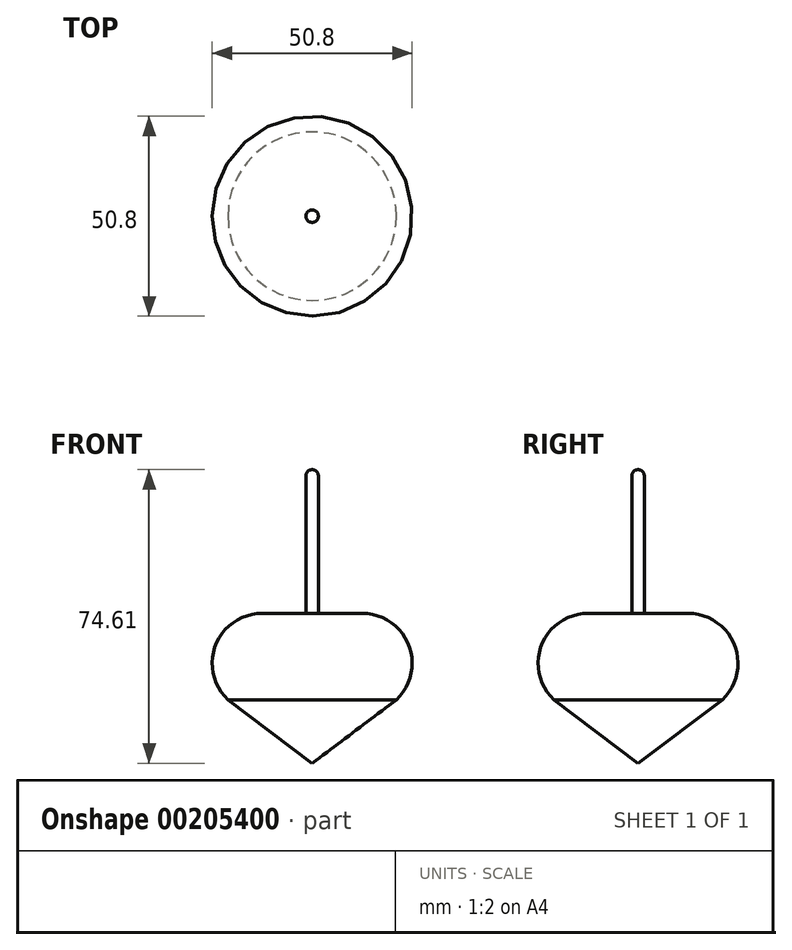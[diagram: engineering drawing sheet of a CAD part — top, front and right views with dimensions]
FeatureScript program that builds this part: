
annotation { "Feature Type Name" : "Feature", "Feature Type Description" : "" }
export const myFeature = defineFeature(function(context is Context, id is Id, definition is map)
    precondition{}
    {
        {
            var Q0;
            Q0=qCreatedBy(makeId("Front.planeOp"),FACE);
            var sketch = newSketch(context, id + "F0", { "sketchPlane" : qUnion([Q0])});
            skLineSegment(sketch, "E0", {"start": v(0, 0) * mm, "end": v(0, 73.03) * mm});
            skArc(sketch, "E1", {"start": v(1.59, 73.03) * mm, "mid": v(1.12, 74.15) * mm, "end": v(0, 74.61) * mm});
            skLineSegment(sketch, "E2", {"start": v(1.59, 73.03) * mm, "end": v(1.59, 38.1) * mm});
            skLineSegment(sketch, "E3", {"start": v(0, 73.03) * mm, "end": v(0, 74.61) * mm});
            skPoint(sketch, "E4", {"position": v(0, 38.1) * mm});
            skLineSegment(sketch, "E5", {"start": v(1.59, 38.1) * mm, "end": v(12.7, 38.1) * mm});
            skArc(sketch, "E6", {"start": v(19.2, 14.5) * mm, "mid": v(24.94, 28.77) * mm, "end": v(12.7, 38.1) * mm});
            skLineSegment(sketch, "E7", {"start": v(0, 0) * mm, "end": v(21.4, 16.15) * mm});
            skSolve(sketch);
        }
        {
            var Q0;
            {var subQ4=sQuery(id+"F0.wireOp",EDGE,"E0");Q0=makeQuery(id+"F0.imprint","IMPRINT",FACE,{"disambiguationData":[TD([[makeQuery(id+"F0.imprint","IMPRINT",EDGE,{"derivedFrom":subQ4}),-1.0]])]});}
            var Q1;
            Q1=sQuery(id+"F0.wireOp",EDGE,"E0");
            revolve(context, id + "F1", {"entities" : qUnion([Q0]), "axis" : qUnion([Q1]), "revolveType" : RevolveType.FULL});
        }
    });
